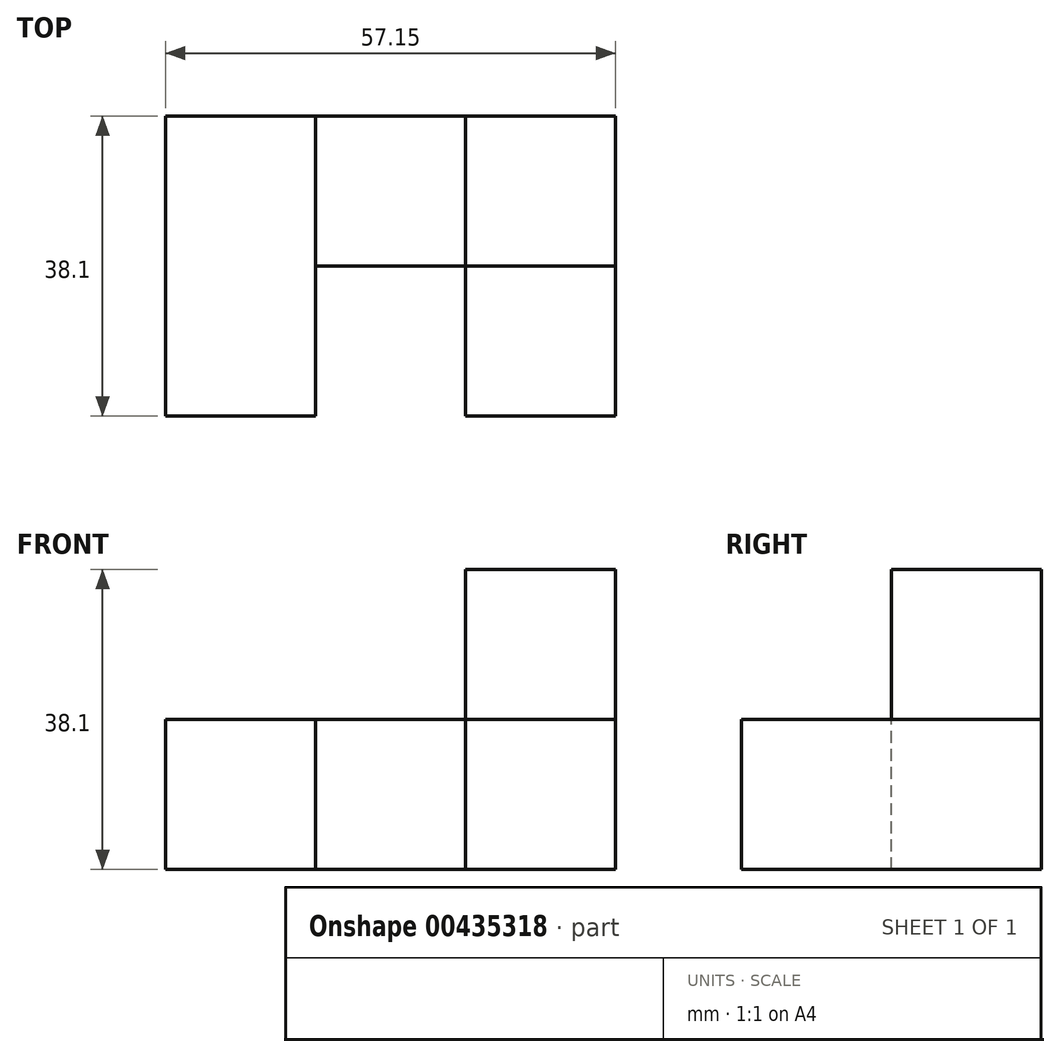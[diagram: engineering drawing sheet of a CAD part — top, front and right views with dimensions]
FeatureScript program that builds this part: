
annotation { "Feature Type Name" : "Feature", "Feature Type Description" : "" }
export const myFeature = defineFeature(function(context is Context, id is Id, definition is map)
    precondition{}
    {
        {
            var Q0;
            Q0=qCreatedBy(makeId("Front.planeOp"),FACE);
            var sketch = newSketch(context, id + "F0", { "sketchPlane" : qUnion([Q0])});
            skLineSegment(sketch, "E0", {"start": v(-44.52, 41.58) * mm, "end": v(-44.52, -57.73) * mm});
            skLineSegment(sketch, "E1", {"start": v(-44.52, -57.73) * mm, "end": v(53.7, -57.73) * mm});
            skLineSegment(sketch, "E2", {"start": v(53.7, -57.73) * mm, "end": v(53.7, 41.58) * mm});
            skLineSegment(sketch, "E3", {"start": v(53.7, 41.58) * mm, "end": v(-44.52, 41.58) * mm});
            skLineSegment(sketch, "E4", {"start": v(-23.91, -38.1) * mm, "end": v(33.24, -38.1) * mm});
            skLineSegment(sketch, "E5", {"start": v(33.24, -38.1) * mm, "end": v(33.24, 0) * mm});
            skLineSegment(sketch, "E6", {"start": v(33.24, 0) * mm, "end": v(14.19, 0) * mm});
            skLineSegment(sketch, "E7", {"start": v(14.19, 0) * mm, "end": v(14.19, -19.05) * mm});
            skPoint(sketch, "E7.endSnap0", {"position": v(33.24, -19.05) * mm});
            skLineSegment(sketch, "E8", {"start": v(14.19, -19.05) * mm, "end": v(-23.91, -19.05) * mm});
            skLineSegment(sketch, "E9", {"start": v(-23.91, -19.05) * mm, "end": v(-23.91, -38.1) * mm});
            skLineSegment(sketch, "E10", {"start": v(-4.86, -19.05) * mm, "end": v(-4.86, -38.1) * mm});
            skPoint(sketch, "E10.endSnap0", {"position": v(4.66, -38.1) * mm});
            skLineSegment(sketch, "E11", {"start": v(-4.86, -38.1) * mm, "end": v(14.19, -38.1) * mm});
            skLineSegment(sketch, "E12", {"start": v(14.19, -38.1) * mm, "end": v(14.19, -19.05) * mm});
            skLineSegment(sketch, "E13", {"start": v(33.24, -19.05) * mm, "end": v(14.19, -19.05) * mm});
            skSolve(sketch);
        }
        {
            var Q0;
            {var subQ0=sQuery(id+"F0.wireOp",EDGE,"E9");Q0=makeQuery(id+"F0.imprint","IMPRINT",FACE,{"disambiguationData":[TD([[makeQuery(id+"F0.imprint","IMPRINT",EDGE,{"derivedFrom":subQ0}),1.0]])]});}
            var Q1;
            {var subQ3=sQuery(id+"F0.wireOp",EDGE,"E12");Q1=makeQuery(id+"F0.imprint","IMPRINT",FACE,{"disambiguationData":[TD([[makeQuery(id+"F0.imprint","IMPRINT",EDGE,{"derivedFrom":subQ3}),-1.0]])]});}
            extrude(context, id + "F1", {"entities" : qUnion([Q0, Q1]), "depth" : 38.1 * mm});
        }
        {
            var Q0;
            {var subQ0=sQuery(id+"F0.wireOp",EDGE,"E6");Q0=makeQuery(id+"F0.imprint","IMPRINT",FACE,{"disambiguationData":[TD([[makeQuery(id+"F0.imprint","IMPRINT",EDGE,{"derivedFrom":subQ0}),1.0]])]});}
            var Q1;
            {var subQ2=sQuery(id+"F0.wireOp",EDGE,"E10");Q1=makeQuery(id+"F0.imprint","IMPRINT",FACE,{"disambiguationData":[TD([[makeQuery(id+"F0.imprint","IMPRINT",EDGE,{"derivedFrom":subQ2}),1.0]])]});}
            extrude(context, id + "F2", {"entities" : qUnion([Q0, Q1]), "depth" : 19.05 * mm});
        }
    });
